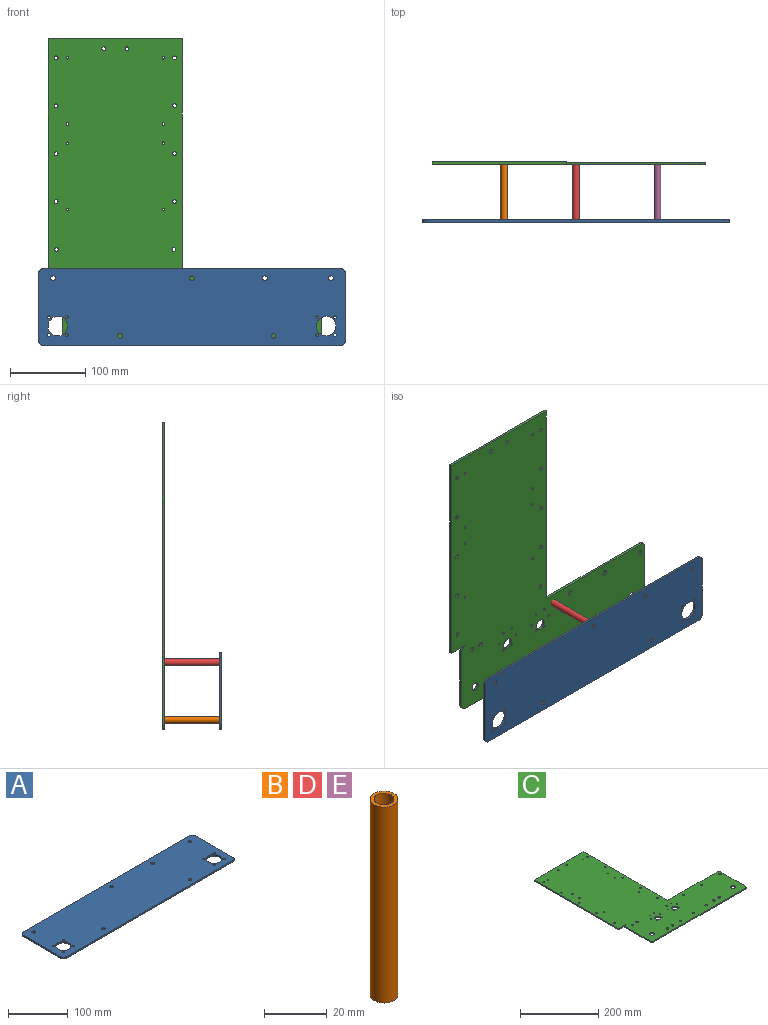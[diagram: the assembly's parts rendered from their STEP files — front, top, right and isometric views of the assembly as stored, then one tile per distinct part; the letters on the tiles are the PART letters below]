
ASSEMBLY  parts=5 mates=2
PART A: 26 faces, bbox 406.4x101.6x3.2 mm
  f0: plane 88.9x3.18mm, normal (1,0,0), area 282.3mm2, adj f4,f5,f8,f9
  f1: plane 393.7x3.18mm, normal (0,1,0), area 1250mm2, adj f4,f5,f6,f9
  f2: plane 88.9x3.18mm, normal (-1,0,0), area 282.3mm2, adj f4,f5,f6,f7
  f3: plane 393.7x3.18mm, normal (0,-1,0), area 1250mm2, adj f4,f5,f7,f8
  f4: plane 406.4x101.6mm, normal (0,0,1), area 39912.5mm2, adj f0,f1,f2,f3,f6,f7,f8,f9
  f5: plane 406.4x101.6mm, normal (0,0,-1), area 39912.5mm2, adj f0,f1,f2,f3,f6,f7,f8,f9
  f6: cylinder r=6.35mm len=6.35mm, axis (0,0,1), area 31.7mm2, adj f1,f2,f4,f5
  f7: cylinder r=6.35mm len=6.35mm, axis (0,0,1), area 31.7mm2, adj f2,f3,f4,f5
  f8: cylinder r=6.35mm len=6.35mm, axis (0,0,1), area 31.7mm2, adj f0,f3,f4,f5
  f9: cylinder r=6.35mm len=6.35mm, axis (0,0,1), area 31.7mm2, adj f0,f1,f4,f5
  f10: cylinder r=13mm len=26mm, axis (0,0,1), area 259.3mm2, adj f4,f5
  f11: cylinder r=13mm len=26mm, axis (0,0,1), area 259.3mm2, adj f4,f5
  f12: cylinder r=3.17mm len=6.35mm, axis (0,0,1), area 63.3mm2, adj f4,f5
  f13: cylinder r=3.17mm len=6.35mm, axis (0,0,1), area 63.3mm2, adj f4,f5
  f14: cylinder r=3.17mm len=6.35mm, axis (0,0,1), area 63.3mm2, adj f4,f5
  f15: cylinder r=3.17mm len=6.35mm, axis (0,0,1), area 63.3mm2, adj f4,f5
  f16: cylinder r=3.17mm len=6.35mm, axis (0,0,1), area 63.3mm2, adj f4,f5
  f17: cylinder r=3.17mm len=6.35mm, axis (0,0,1), area 63.3mm2, adj f4,f5
  f18: cylinder r=1.91mm len=3.81mm, axis (0,0,1), area 38mm2, adj f4,f5
  f19: cylinder r=1.91mm len=3.81mm, axis (0,0,1), area 38mm2, adj f4,f5
  f20: cylinder r=1.91mm len=3.81mm, axis (0,0,1), area 38mm2, adj f4,f5
  f21: cylinder r=1.91mm len=3.81mm, axis (0,0,1), area 38mm2, adj f4,f5
  f22: cylinder r=1.91mm len=3.81mm, axis (0,0,1), area 38mm2, adj f4,f5
  f23: cylinder r=1.91mm len=3.81mm, axis (0,0,1), area 38mm2, adj f4,f5
  f24: cylinder r=1.91mm len=3.81mm, axis (0,0,1), area 38mm2, adj f4,f5
  f25: cylinder r=1.91mm len=3.81mm, axis (0,0,1), area 38mm2, adj f4,f5
PART B: 4 faces, bbox 8.9x8.9x76.2 mm
  f0: cylinder r=3.17mm len=76.2mm, axis (0,0,-1), area 1520.1mm2, adj f2,f3
  f1: cylinder r=4.45mm len=76.2mm, axis (0,0,-1), area 2128.2mm2, adj f2,f3
  f2: plane 8.89x8.89mm, normal (0,0,1), area 30.4mm2, adj f0,f1
  f3: plane 8.89x8.89mm, normal (0,0,-1), area 30.4mm2, adj f0,f1
PART C: 62 faces, bbox 362x406.4x3.2 mm
  f0: plane 406.4x361.95mm, normal (0,0,1), area 87630.8mm2, adj f2,f3,f4,f5,f6,f7,f8,f9
  f1: plane 406.4x361.95mm, normal (0,0,-1), area 87630.8mm2, adj f2,f3,f4,f5,f6,f7,f8,f9
  f2: plane 177.8x3.18mm, normal (0,1,0), area 564.5mm2, adj f0,f1,f37,f51
  f3: plane 88.9x3.18mm, normal (1,0,0), area 282.3mm2, adj f0,f1,f8,f9
  f4: plane 88.9x3.18mm, normal (-1,0,0), area 282.3mm2, adj f0,f1,f6,f7
  f5: plane 330.2x3.18mm, normal (0,-1,0), area 1048.4mm2, adj f0,f1,f7,f8
  f6: cylinder r=6.35mm len=6.35mm, axis (0,0,1), area 31.7mm2, adj f0,f1,f4,f36
  f7: cylinder r=6.35mm len=6.35mm, axis (0,0,1), area 31.7mm2, adj f0,f1,f4,f5
  f8: cylinder r=6.35mm len=6.35mm, axis (0,0,1), area 31.7mm2, adj f0,f1,f3,f5
  f9: cylinder r=6.35mm len=6.35mm, axis (0,0,1), area 31.7mm2, adj f0,f1,f3,f50
  f10: cylinder r=6mm len=12mm, axis (0,0,1), area 119.7mm2, adj f0,f1
  f11: cylinder r=6mm len=12mm, axis (0,0,1), area 119.7mm2, adj f0,f1
  f12: cylinder r=3.17mm len=6.35mm, axis (0,0,1), area 63.3mm2, adj f0,f1
  f13: cylinder r=3.17mm len=6.35mm, axis (0,0,1), area 63.3mm2, adj f0,f1
  f14: cylinder r=3.17mm len=6.35mm, axis (0,0,1), area 63.3mm2, adj f0,f1
  f15: cylinder r=3.17mm len=6.35mm, axis (0,0,1), area 63.3mm2, adj f0,f1
  f16: cylinder r=3.17mm len=6.35mm, axis (0,0,1), area 63.3mm2, adj f0,f1
  f17: cylinder r=3.17mm len=6.35mm, axis (0,0,1), area 63.3mm2, adj f0,f1
  f18: cylinder r=3.17mm len=6.35mm, axis (0,0,1), area 63.3mm2, adj f0,f1
  f19: cylinder r=3.17mm len=6.35mm, axis (0,0,1), area 63.3mm2, adj f0,f1
  f20: cylinder r=3.17mm len=6.35mm, axis (0,0,1), area 63.3mm2, adj f0,f1
  f21: cylinder r=3.17mm len=6.35mm, axis (0,0,1), area 63.3mm2, adj f0,f1
  f22: cylinder r=7.51mm len=15.01mm, axis (0,0,1), area 149.7mm2, adj f0,f1
  f23: cylinder r=7.5mm len=15mm, axis (0,0,1), area 149.6mm2, adj f0,f1
  f24: cylinder r=1.59mm len=3.18mm, axis (0,0,1), area 31.7mm2, adj f0,f1
  f25: cylinder r=1.59mm len=3.18mm, axis (0,0,1), area 31.7mm2, adj f0,f1
  f26: cylinder r=1.59mm len=3.18mm, axis (0,0,1), area 31.7mm2, adj f0,f1
  f27: cylinder r=1.59mm len=3.18mm, axis (0,0,1), area 31.7mm2, adj f0,f1
  f28: cylinder r=1.59mm len=3.18mm, axis (0,0,1), area 31.7mm2, adj f0,f1
  f29: cylinder r=1.59mm len=3.18mm, axis (0,0,1), area 31.7mm2, adj f0,f1
  f30: cylinder r=1.59mm len=3.18mm, axis (0,0,1), area 31.7mm2, adj f0,f1
  f31: cylinder r=1.59mm len=3.18mm, axis (0,0,1), area 31.7mm2, adj f0,f1
  f32: cylinder r=1.59mm len=3.18mm, axis (0,0,1), area 31.7mm2, adj f0,f1
  f33: cylinder r=1.59mm len=3.18mm, axis (0,0,1), area 31.7mm2, adj f0,f1
  f34: cylinder r=1.59mm len=3.18mm, axis (0,0,1), area 31.7mm2, adj f0,f1
  f35: cylinder r=1.59mm len=3.18mm, axis (0,0,1), area 31.7mm2, adj f0,f1
  f36: plane 25.4x3.18mm, normal (0,-1,0), area 80.6mm2, adj f0,f1,f6,f37
  f37: plane 304.8x3.18mm, normal (-1,0,0), area 967.7mm2, adj f0,f1,f2,f36
  f38: cylinder r=1.65mm len=3.3mm, axis (0,0,1), area 32.9mm2, adj f0,f1
  f39: cylinder r=2.54mm len=5.08mm, axis (0,0,1), area 50.7mm2, adj f0,f1
  f40: cylinder r=1.65mm len=3.3mm, axis (0,0,1), area 32.9mm2, adj f0,f1
  f41: cylinder r=1.65mm len=3.3mm, axis (0,0,1), area 32.9mm2, adj f0,f1
  f42: cylinder r=1.65mm len=3.3mm, axis (0,0,1), area 32.9mm2, adj f0,f1
  f43: cylinder r=1.65mm len=3.3mm, axis (0,0,1), area 32.9mm2, adj f0,f1
  f44: cylinder r=1.65mm len=3.3mm, axis (0,0,1), area 32.9mm2, adj f0,f1
  f45: cylinder r=1.65mm len=3.3mm, axis (0,0,1), area 32.9mm2, adj f0,f1
  f46: cylinder r=1.65mm len=3.3mm, axis (0,0,1), area 32.9mm2, adj f0,f1
  f47: cylinder r=2.54mm len=5.08mm, axis (0,0,1), area 50.7mm2, adj f0,f1
  f48: cylinder r=3.17mm len=6.35mm, axis (0,0,1), area 63.3mm2, adj f0,f1
  f49: cylinder r=3.17mm len=6.35mm, axis (0,0,1), area 63.3mm2, adj f0,f1
  f50: plane 177.8x3.18mm, normal (0,1,0), area 564.5mm2, adj f0,f1,f9,f51
  f51: plane 304.8x3.18mm, normal (1,0,0), area 967.7mm2, adj f0,f1,f2,f50
  f52: cylinder r=2.54mm len=5.08mm, axis (0,0,1), area 50.7mm2, adj f0,f1
  f53: cylinder r=2.54mm len=5.08mm, axis (0,0,1), area 50.7mm2, adj f0,f1
  f54: cylinder r=2.54mm len=5.08mm, axis (0,0,1), area 50.7mm2, adj f0,f1
  f55: cylinder r=2.54mm len=5.08mm, axis (0,0,1), area 50.7mm2, adj f0,f1
  f56: cylinder r=2.54mm len=5.08mm, axis (0,0,1), area 50.7mm2, adj f0,f1
  f57: cylinder r=2.54mm len=5.08mm, axis (0,0,1), area 50.7mm2, adj f0,f1
  f58: cylinder r=2.54mm len=5.08mm, axis (0,0,1), area 50.7mm2, adj f0,f1
  f59: cylinder r=2.54mm len=5.08mm, axis (0,0,1), area 50.7mm2, adj f0,f1
  f60: cylinder r=2.54mm len=5.08mm, axis (0,0,1), area 50.7mm2, adj f0,f1
  f61: cylinder r=2.54mm len=5.08mm, axis (0,0,1), area 50.7mm2, adj f0,f1
PART D: same geometry as B
PART E: same geometry as B
PLACE A rot(axis=(1,0,0),90deg) t=(0.99,-15.02,19.84)mm
PLACE B rot(axis=(1,0,0),90deg) t=(-44.04,61.18,-35.75)mm
PLACE C rot(axis=(1,0,0),90deg) t=(0.99,61.18,19.84)mm
PLACE D rot(axis=(0.58,-0.58,0.58),120deg) t=(18.4,61.18,108.17)mm
PLACE E rot(axis=(1,0,0),90deg) t=(159.16,61.18,-35.91)mm
MATE cylindrical E.f0 <-> A.f17  axis (0,-1,0) through (108.94,-15.02,-18.5)mm
MATE cylindrical B.f0 <-> A.f16  axis (0,-1,0) through (-94.26,-15.02,-18.34)mm
